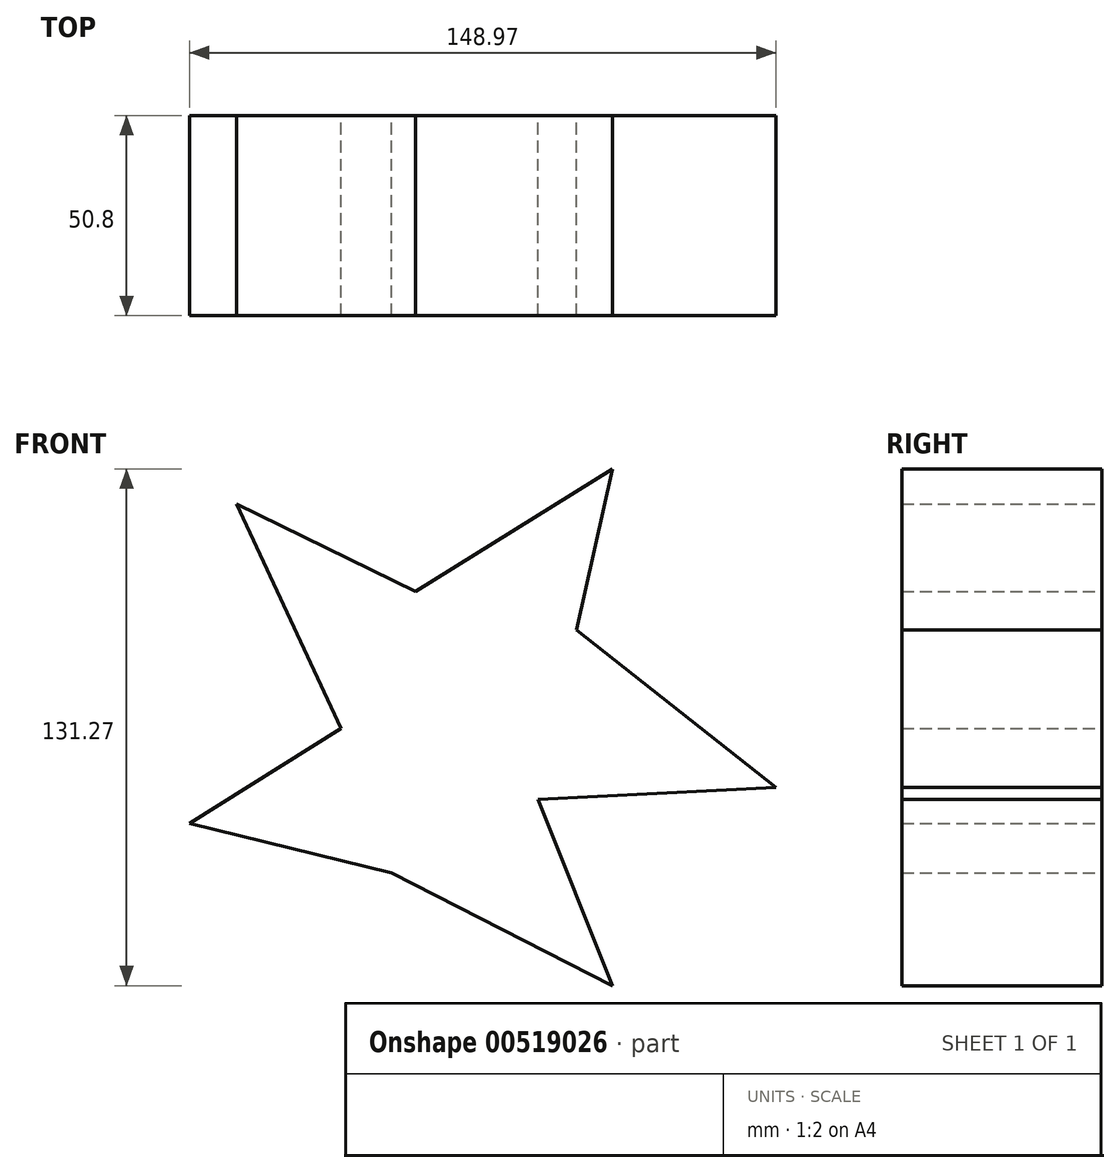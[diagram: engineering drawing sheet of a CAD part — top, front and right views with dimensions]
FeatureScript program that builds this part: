
annotation { "Feature Type Name" : "Feature", "Feature Type Description" : "" }
export const myFeature = defineFeature(function(context is Context, id is Id, definition is map)
    precondition{}
    {
        {
            var Q0;
            Q0=qCreatedBy(makeId("Front.planeOp"),FACE);
            var sketch = newSketch(context, id + "F0", { "sketchPlane" : qUnion([Q0])});
            skFitSpline(sketch, "E0", {"points": [v(28.08, 16.79) * mm, v(37.24, 57.7) * mm], "startDerivative": vector(9.16, 40.9) * mm, "endDerivative": vector(9.16, 40.9) * mm});
            skFitSpline(sketch, "E1", {"points": [v(37.24, 57.7) * mm, v(-12.82, 26.56) * mm], "startDerivative": vector(-50.06, -31.14) * mm, "endDerivative": vector(-50.06, -31.14) * mm});
            skFitSpline(sketch, "E2", {"points": [v(-12.82, 26.56) * mm, v(-58.3, 48.84) * mm], "startDerivative": vector(-45.48, 22.28) * mm, "endDerivative": vector(-45.48, 22.28) * mm});
            skFitSpline(sketch, "E3", {"points": [v(-58.3, 48.84) * mm, v(-31.75, -8.24) * mm], "startDerivative": vector(26.56, -57.08) * mm, "endDerivative": vector(26.56, -57.08) * mm});
            skFitSpline(sketch, "E4", {"points": [v(-31.75, -8.24) * mm, v(-70.21, -32.36) * mm], "startDerivative": vector(-38.46, -24.12) * mm, "endDerivative": vector(-38.46, -24.12) * mm});
            skFitSpline(sketch, "E5", {"points": [v(-70.21, -32.36) * mm, v(-18.93, -44.87) * mm], "startDerivative": vector(51.28, -12.52) * mm, "endDerivative": vector(51.28, -12.52) * mm});
            skFitSpline(sketch, "E6", {"points": [v(-18.93, -44.87) * mm, v(37.24, -73.57) * mm], "startDerivative": vector(56.17, -28.7) * mm, "endDerivative": vector(56.17, -28.7) * mm});
            skFitSpline(sketch, "E7", {"points": [v(37.24, -73.57) * mm, v(18.32, -26.25) * mm], "startDerivative": vector(-18.93, 47.32) * mm, "endDerivative": vector(-18.93, 47.32) * mm});
            skFitSpline(sketch, "E8", {"points": [v(18.32, -26.25) * mm, v(78.76, -23.2) * mm], "startDerivative": vector(60.44, 3.05) * mm, "endDerivative": vector(60.44, 3.05) * mm});
            skFitSpline(sketch, "E9", {"points": [v(78.76, -23.2) * mm, v(28.08, 16.79) * mm], "startDerivative": vector(-50.67, 40) * mm, "endDerivative": vector(-50.67, 40) * mm});
            skSolve(sketch);
        }
        {
            var Q0;
            Q0=makeQuery(id+"F0.imprint","IMPRINT",FACE,{"disambiguationData":[TD([[makeQuery(id+"F0.imprint","IMPRINT",EDGE,{"derivedFrom":sQuery(id+"F0.wireOp",EDGE,"E0")}),1.0]])]});
            extrude(context, id + "F1", {"entities" : qUnion([Q0]), "depth" : 50.8 * mm, "offsetDistance" : 25.4 * mm});
        }
    });
